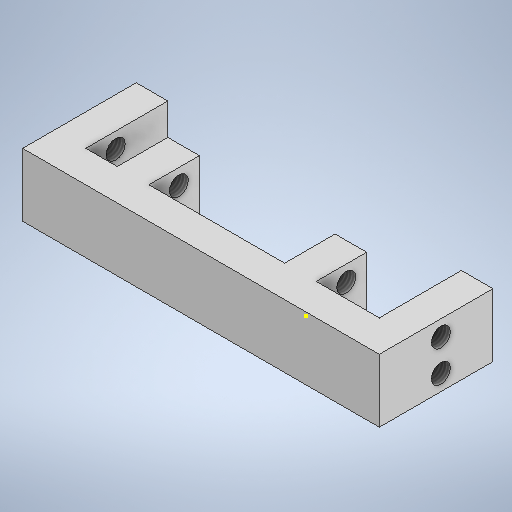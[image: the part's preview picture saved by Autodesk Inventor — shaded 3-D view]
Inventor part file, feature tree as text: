
AUTODESK INVENTOR PART (.ipt)
format: ipt  version: 2025.2 (Build 292293000, 293)  size: 305,152 bytes
history: native  units: mm
features: thread x8, sketch x4, extrude x3
ambient origin geometry x8: Origin, YZ Plane, XZ Plane, XY Plane, X Axis, Y Axis, Z Axis, Center Point
bodies: Solid1 (feature_tree)
feature tree (15):
  extrude  "Extrusion1"  Depth=5.0mm
  extrude  "Extrusion2"  Depth=8.0mm
  thread  "Thread1"  [1 undecoded]
  thread  "Thread2"  [1 undecoded]
  thread  "Thread3"  [1 undecoded]
  thread  "Thread4"  [1 undecoded]
  thread  "Thread5"  [1 undecoded]
  thread  "Thread6"  [1 undecoded]
  thread  "Thread7"  [1 undecoded]
  thread  "Thread8"  [1 undecoded]
  extrude  "Extrusion3"  Depth=60.0mm TaperAngle=0.0deg
  sketch  "Sketch4"  dims[d16=5.0mm d17=0.0mm d18=5.0mm d19=0.0mm d20=5.0mm d21=0.0mm d22=5.0mm d23=0.0mm d24=5.0mm d25=0.0mm d26=5.0mm d27=0.0mm d28=5.0mm d29=0.0mm d30=5.0mm d31=0.0mm d32=5.0mm d33=0.0mm d34=5.0mm d35=0.872665mm]
  sketch  "Sketch1"  dims[d0=46.5mm d1=5.0mm]
  sketch  "Sketch2"  dims[d2=5.0mm d3=8.0mm d4=5.0mm d5=5.0mm d6=5.0mm d7=8.0mm d8=10.0mm d9=5.0mm d10=10.0mm d11=0.0mm d12=3.0mm]
  sketch  "Sketch3"  dims[d13=3.0mm d14=60.0mm d15=0.0mm]
note: 8 required parameter values undecoded (feature->parameter linkage not recoverable at this tier; creation-order binding heuristic only, values carry confidence <= 0.55)
